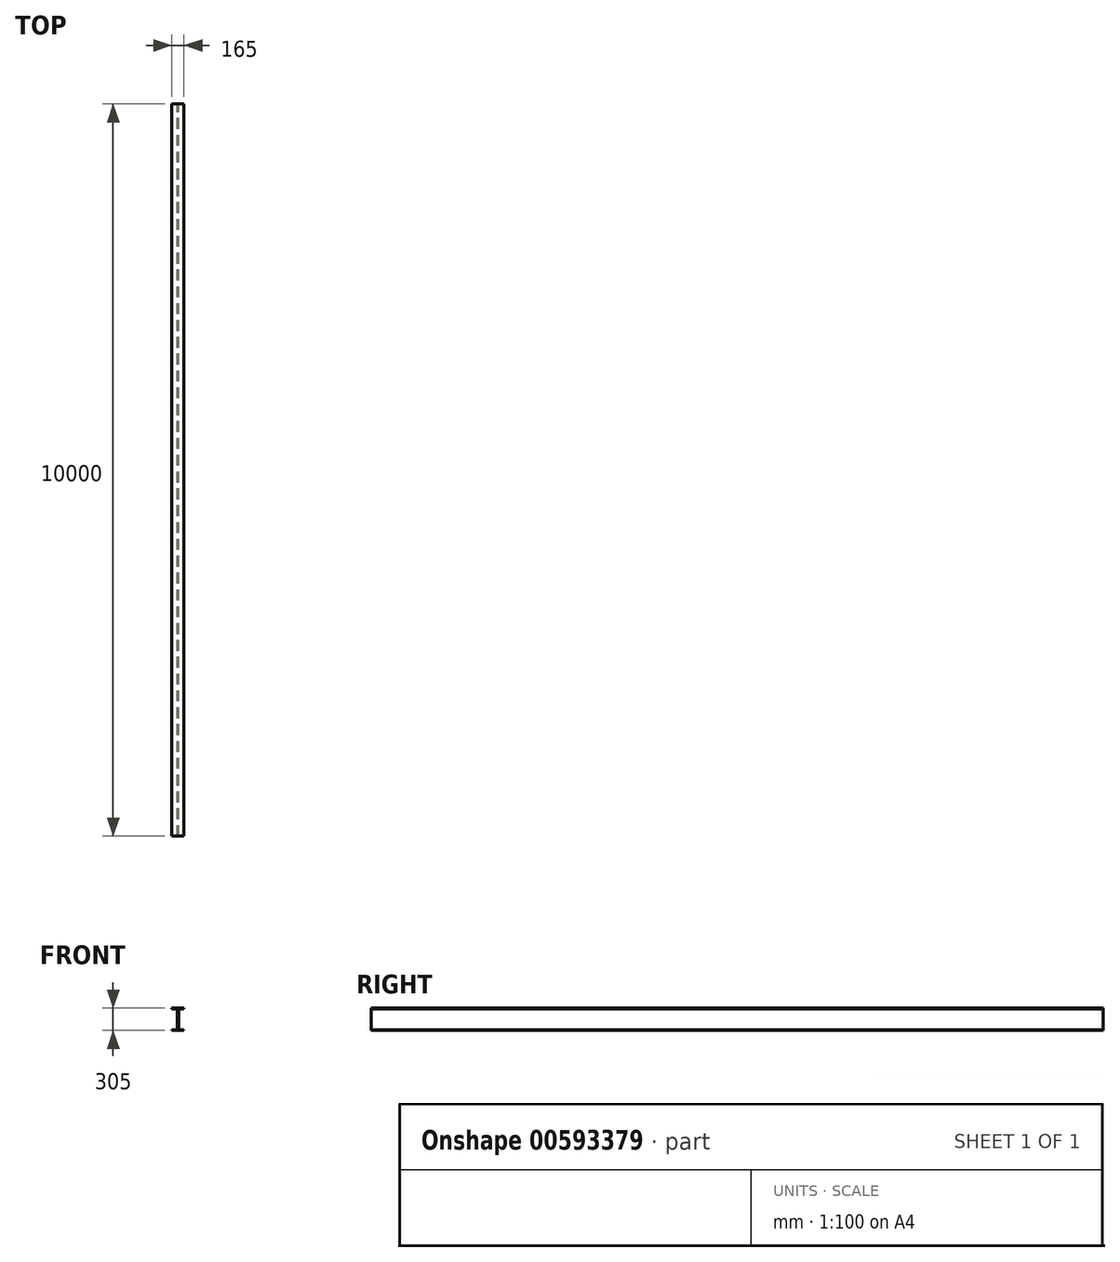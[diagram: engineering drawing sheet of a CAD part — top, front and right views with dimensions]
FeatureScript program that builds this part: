
annotation { "Feature Type Name" : "Feature", "Feature Type Description" : "" }
export const myFeature = defineFeature(function(context is Context, id is Id, definition is map)
    precondition{}
    {
        {
            var Q0;
            Q0=qCreatedBy(makeId("Front.planeOp"),FACE);
            var sketch = newSketch(context, id + "F0", { "sketchPlane" : qUnion([Q0])});
            skLineSegment(sketch, "E0.bottom", {"start": v(-81.76, 138.97) * mm, "end": v(83.24, 138.97) * mm});
            skLineSegment(sketch, "E0.left", {"start": v(-81.76, 138.97) * mm, "end": v(-81.76, 128.97) * mm});
            skLineSegment(sketch, "E0.right", {"start": v(83.24, 138.97) * mm, "end": v(83.24, 128.97) * mm});
            skLineSegment(sketch, "E1.left", {"start": v(-6.76, 118.97) * mm, "end": v(-6.76, -146.03) * mm});
            skLineSegment(sketch, "E1.right", {"start": v(8.24, 118.97) * mm, "end": v(8.24, -146.03) * mm});
            skLineSegment(sketch, "E2.left", {"start": v(83.24, -156.03) * mm, "end": v(83.24, -166.03) * mm});
            skLineSegment(sketch, "E3.trimOffspring", {"start": v(18.24, 128.97) * mm, "end": v(83.24, 128.97) * mm});
            skLineSegment(sketch, "E4", {"start": v(-81.76, 128.97) * mm, "end": v(-16.76, 128.97) * mm});
            skLineSegment(sketch, "E5", {"start": v(18.24, -156.03) * mm, "end": v(83.24, -156.03) * mm});
            skLineSegment(sketch, "E6", {"start": v(-16.76, -156.03) * mm, "end": v(-81.76, -156.03) * mm});
            skLineSegment(sketch, "E7", {"start": v(-81.76, -156.03) * mm, "end": v(-81.76, -166.03) * mm});
            skLineSegment(sketch, "E8", {"start": v(-81.76, -166.03) * mm, "end": v(83.24, -166.03) * mm});
            skArc(sketch, "E9", {"start": v(-6.76, 118.97) * mm, "mid": v(-9.69, 126.04) * mm, "end": v(-16.76, 128.97) * mm});
            skArc(sketch, "E10", {"start": v(18.24, 128.97) * mm, "mid": v(11.17, 126.04) * mm, "end": v(8.24, 118.97) * mm});
            skArc(sketch, "E11", {"start": v(8.24, -146.03) * mm, "mid": v(11.17, -153.1) * mm, "end": v(18.24, -156.03) * mm});
            skArc(sketch, "E12", {"start": v(-16.76, -156.03) * mm, "mid": v(-9.69, -153.1) * mm, "end": v(-6.76, -146.03) * mm});
            skSolve(sketch);
        }
        {
            var Q0;
            Q0 = qSketchRegion(id + "F0", true);
            extrude(context, id + "F1", {"entities" : qUnion([Q0]), "depth" : 5000 * mm, "offsetDistance" : 25 * mm, "hasSecondDirection" : true, "secondDirectionOppositeDirection" : true, "secondDirectionDepth" : 5000 * mm});
        }
    });
